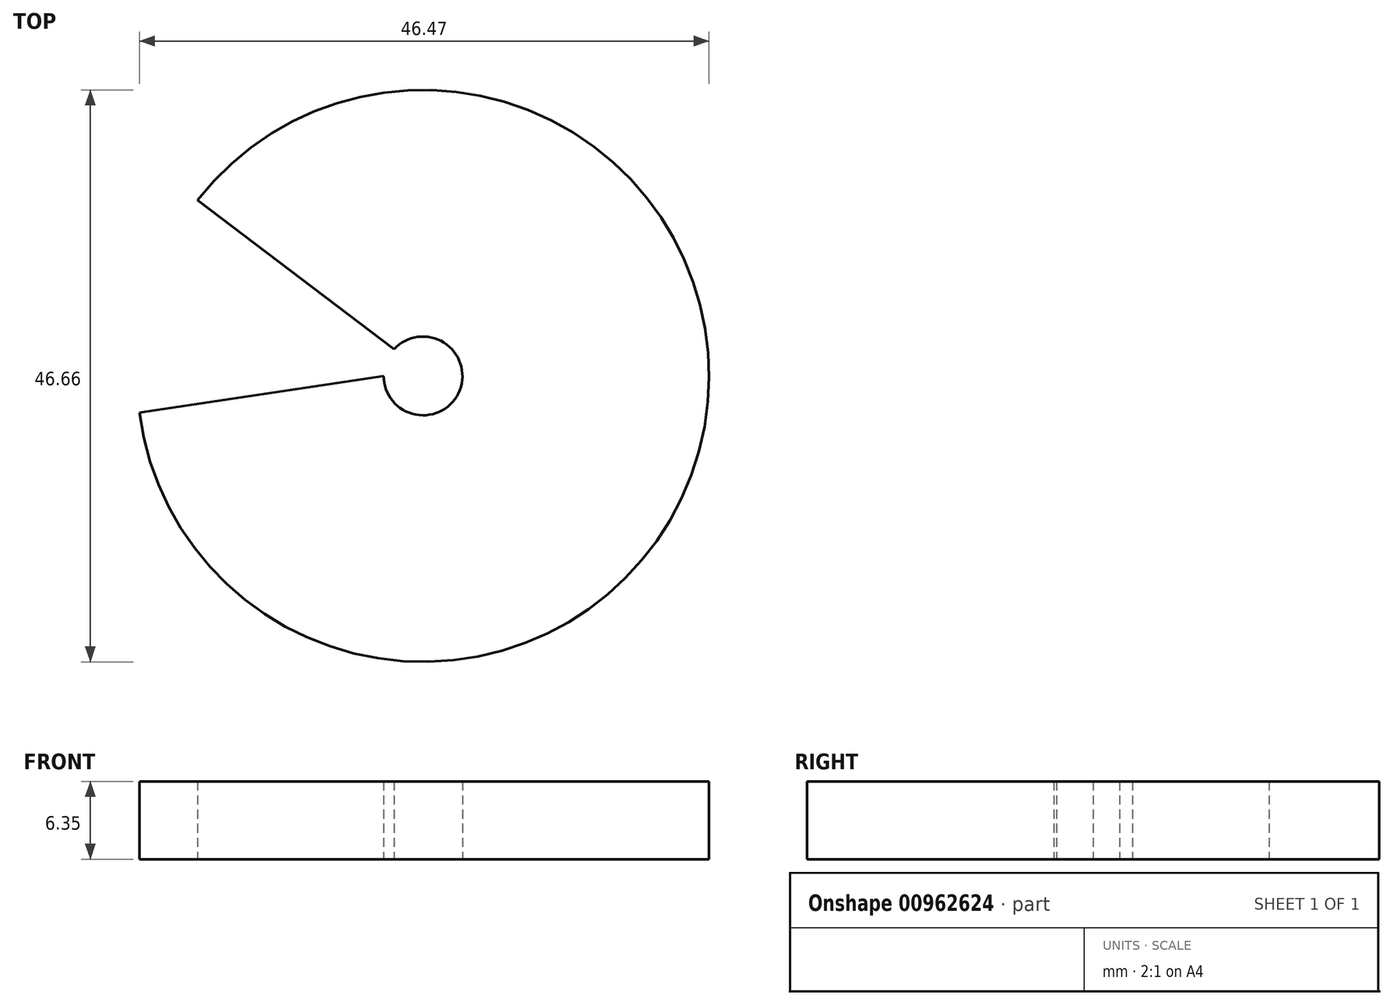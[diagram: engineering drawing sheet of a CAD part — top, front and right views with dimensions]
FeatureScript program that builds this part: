
annotation { "Feature Type Name" : "Feature", "Feature Type Description" : "" }
export const myFeature = defineFeature(function(context is Context, id is Id, definition is map)
    precondition{}
    {
        {
            var Q0;
            Q0=qCreatedBy(makeId("Top.planeOp"),FACE);
            var sketch = newSketch(context, id + "F0", { "sketchPlane" : qUnion([Q0])});
            skCircle(sketch, "E0", {"center": v(0, 0) * mm, "radius": 26.5 * mm});
            skCircle(sketch, "E1", {"center": v(0, 0) * mm, "radius": 23.33 * mm});
            skCircle(sketch, "E2", {"center": v(0, 0) * mm, "radius": 3.21 * mm});
            skLineSegment(sketch, "E3", {"start": v(-23.14, -2.98) * mm, "end": v(-3.21, 0) * mm});
            skLineSegment(sketch, "E4", {"start": v(-3.21, 0) * mm, "end": v(-2.36, 2.17) * mm});
            skLineSegment(sketch, "E5", {"start": v(-2.36, 2.17) * mm, "end": v(-18.4, 14.34) * mm});
            skSolve(sketch);
        }
        {
            var Q0;
            {var subQ0=sQuery(id+"F0.wireOp",EDGE,"E3");Q0=makeQuery(id+"F0.imprint","IMPRINT",FACE,{"disambiguationData":[TD([[makeQuery(id+"F0.imprint","IMPRINT",EDGE,{"derivedFrom":subQ0}),-1.0]])]});}
            extrude(context, id + "F1", {"entities" : qUnion([Q0]), "depth" : 6.35 * mm, "offsetDistance" : 25.4 * mm});
        }
    });
